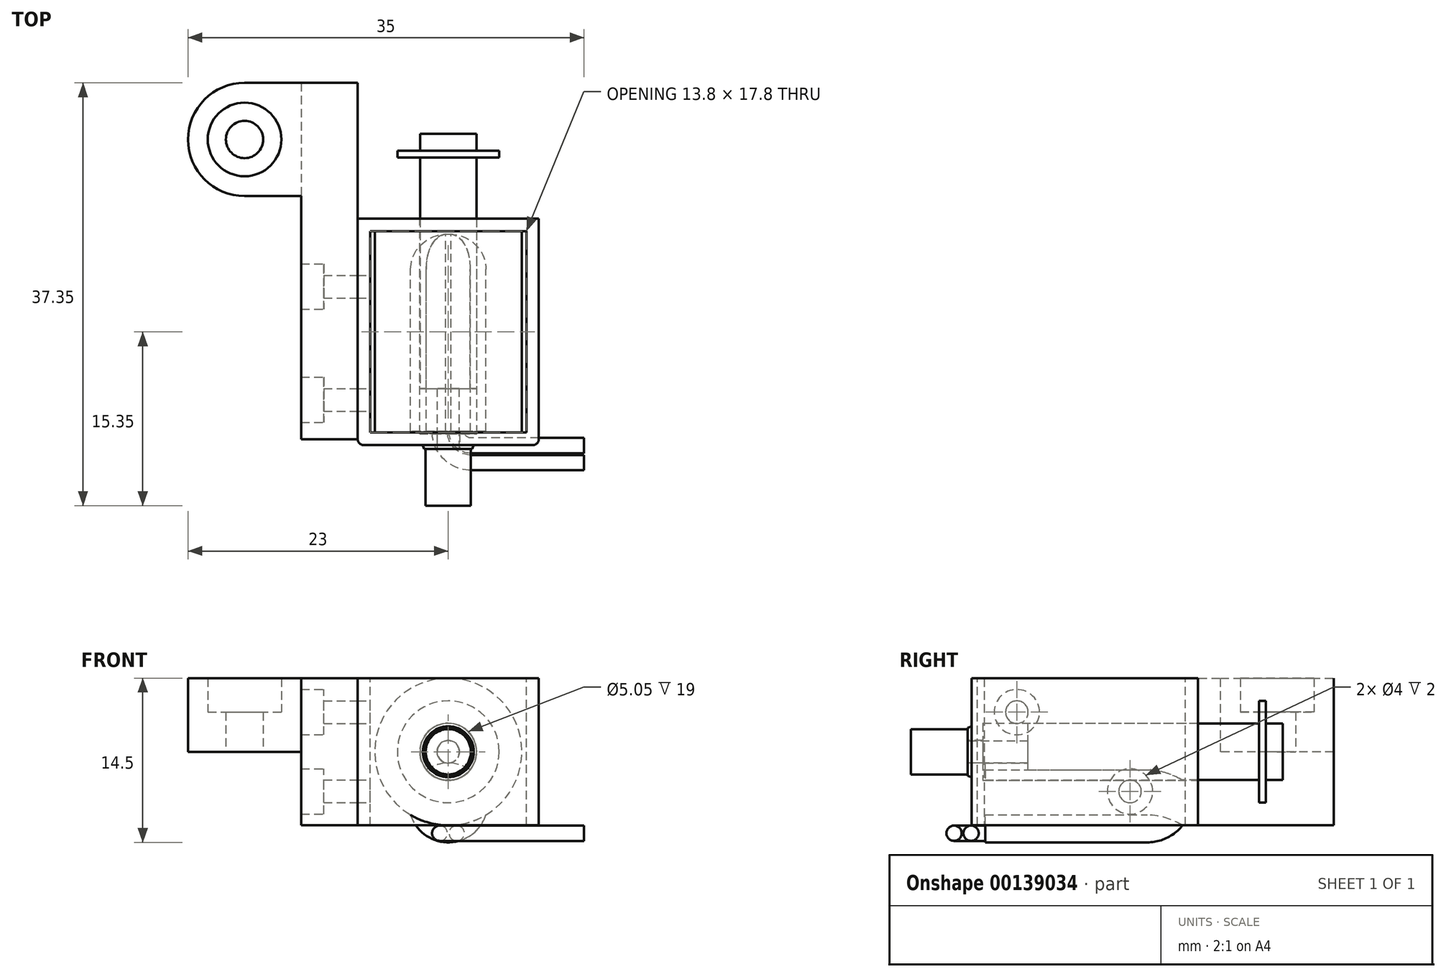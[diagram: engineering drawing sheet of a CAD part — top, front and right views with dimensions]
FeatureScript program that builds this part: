
annotation { "Feature Type Name" : "Feature", "Feature Type Description" : "" }
export const myFeature = defineFeature(function(context is Context, id is Id, definition is map)
    precondition{}
    {
        {
            var Q0;
            Q0=qCreatedBy(makeId("Front.planeOp"),FACE);
            var sketch = newSketch(context, id + "F0", { "sketchPlane" : qUnion([Q0])});
            skLineSegment(sketch, "E0.bottom", {"start": v(8, -6.5) * mm, "end": v(-8, -6.5) * mm});
            skLineSegment(sketch, "E0.top", {"start": v(8, 6.5) * mm, "end": v(-8, 6.5) * mm});
            skLineSegment(sketch, "E0.left", {"start": v(8, -6.5) * mm, "end": v(8, 6.5) * mm});
            skLineSegment(sketch, "E0.right", {"start": v(-8, -6.5) * mm, "end": v(-8, 6.5) * mm});
            skPoint(sketch, "E0.middle", {"position": v(0, 0) * mm});
            skSolve(sketch);
        }
        {
            var Q0;
            Q0 = qSketchRegion(id + "F0", true);
            extrude(context, id + "F1", {"entities" : qUnion([Q0]), "oppositeDirection" : true, "depth" : 20 * mm});
        }
        {
            var Q0;
            Q0=makeQuery(id+"F1.opExtrude","CAP_EDGE",EDGE,{"disambiguationData":[OSD([sQuery(id+"F0.wireOp",EDGE,"E0.right")])],"isStart":true});
            var Q1;
            Q1=makeQuery(id+"F1.opExtrude","CAP_EDGE",EDGE,{"disambiguationData":[OSD([sQuery(id+"F0.wireOp",EDGE,"E0.left")])],"isStart":true});
            fillet(context, id + "F2", {"entities" : qUnion([Q0, Q1]), "radius" : 0.5 * mm, "tangentPropagation" : true, "allowEdgeOverflow" : false});
        }
        {
            var Q0;
            Q0=makeQuery(id+"F1.opExtrude","SWEPT_FACE",FACE,{"disambiguationData":[OSD([sQuery(id+"F0.wireOp",EDGE,"E0.top")])]});
            var Q1;
            Q1=makeQuery(id+"F1.opExtrude","SWEPT_FACE",FACE,{"disambiguationData":[OSD([sQuery(id+"F0.wireOp",EDGE,"E0.bottom")])]});
            shell(context, id + "F3", {"entities" : qUnion([Q0, Q1]), "thickness" : 1.1 * mm});
        }
        {
            var Q0;
            {var subQ0=sQuery(id+"F0.wireOp",EDGE,"E0.right");var subQ1=sQuery(id+"F0.wireOp",EDGE,"E0.left");var subQ2=sQuery(id+"F0.wireOp",EDGE,"E0.top");var subQ3=sQuery(id+"F0.wireOp",EDGE,"E0.bottom");Q0=makeQuery(id+"F3.opShell","OFFSET_FACE",FACE,{"disambiguationData":[OSD([subQ3,subQ2,subQ1,subQ0]),TDD([makeQuery(id+"F1.opExtrude","CAP_FACE",FACE,{"disambiguationData":[OSD([subQ3,subQ2,subQ1,subQ0])],"isStart":true})])]});}
            var sketch = newSketch(context, id + "F4", { "sketchPlane" : qUnion([Q0])});
            skCircle(sketch, "E1", {"center": v(0, 0) * mm, "radius": 6.5 * mm});
            skSolve(sketch);
        }
        {
            var Q0;
            Q0 = qSketchRegion(id + "F4", true);
            extrude(context, id + "F5", {"entities" : qUnion([Q0]), "operationType" : NewBodyOperationType.ADD, "endBound" : BoundingType.UP_TO_NEXT, "depth" : 25 * mm});
        }
        {
            var Q0;
            Q0=makeQuery(id+"F1.opExtrude","CAP_FACE",FACE,{"disambiguationData":[OSD([sQuery(id+"F0.wireOp",EDGE,"E0.bottom"),sQuery(id+"F0.wireOp",EDGE,"E0.top"),sQuery(id+"F0.wireOp",EDGE,"E0.left"),sQuery(id+"F0.wireOp",EDGE,"E0.right")])],"isStart":true});
            var sketch = newSketch(context, id + "F6", { "sketchPlane" : qUnion([Q0])});
            skCircle(sketch, "E2", {"center": v(0, 0) * mm, "radius": 1 * mm});
            skSolve(sketch);
        }
        {
            var Q0;
            Q0=makeQuery(id+"F6.imprint","IMPRINT",FACE,{"disambiguationData":[TD([[makeQuery(id+"F6.imprint","IMPRINT",EDGE,{"derivedFrom":sQuery(id+"F6.wireOp",EDGE,"E2")}),-1.0]])]});
            var sketch = newSketch(context, id + "F7", { "sketchPlane" : qUnion([Q0])});
            skCircle(sketch, "E3", {"center": v(0, 0) * mm, "radius": 2.25 * mm});
            skSolve(sketch);
        }
        {
            var Q0;
            Q0 = qSketchRegion(id + "F7", true);
            extrude(context, id + "F8", {"entities" : qUnion([Q0]), "operationType" : NewBodyOperationType.ADD, "depth" : 0.35 * mm, "hasDraft" : true, "draftAngle" : 20 * degree, "draftPullDirection" : true});
        }
        {
            var Q0;
            Q0 = qSketchRegion(id + "F6", true);
            extrude(context, id + "F9", {"entities" : qUnion([Q0]), "operationType" : NewBodyOperationType.REMOVE, "endBound" : BoundingType.THROUGH_ALL, "oppositeDirection" : true, "depth" : 25 * mm, "hasSecondDirection" : true, "secondDirectionBound" : BoundingType.THROUGH_ALL, "secondDirectionOppositeDirection" : false, "secondDirectionDepth" : 25 * mm});
        }
        {
            var Q0;
            Q0=makeQuery(id+"F1.opExtrude","CAP_FACE",FACE,{"disambiguationData":[OSD([sQuery(id+"F0.wireOp",EDGE,"E0.bottom"),sQuery(id+"F0.wireOp",EDGE,"E0.top"),sQuery(id+"F0.wireOp",EDGE,"E0.left"),sQuery(id+"F0.wireOp",EDGE,"E0.right")])],"isStart":false});
            var sketch = newSketch(context, id + "F10", { "sketchPlane" : qUnion([Q0])});
            skCircle(sketch, "E4", {"center": v(0, 0) * mm, "radius": 2.52 * mm});
            skSolve(sketch);
        }
        {
            var Q0;
            Q0 = qSketchRegion(id + "F10", true);
            extrude(context, id + "F11", {"entities" : qUnion([Q0]), "operationType" : NewBodyOperationType.REMOVE, "oppositeDirection" : true, "depth" : 19 * mm});
        }
        {
            var Q0;
            Q0=makeQuery(id+"F1.opExtrude","CAP_FACE",FACE,{"disambiguationData":[OSD([sQuery(id+"F0.wireOp",EDGE,"E0.bottom"),sQuery(id+"F0.wireOp",EDGE,"E0.top"),sQuery(id+"F0.wireOp",EDGE,"E0.left"),sQuery(id+"F0.wireOp",EDGE,"E0.right")])],"isStart":false});
            var sketch = newSketch(context, id + "F12", { "sketchPlane" : qUnion([Q0])});
            skCircle(sketch, "E5", {"center": v(0, 0) * mm, "radius": 2.5 * mm});
            skSolve(sketch);
        }
        {
            var Q0;
            Q0 = qSketchRegion(id + "F12", true);
            extrude(context, id + "F13", {"entities" : qUnion([Q0]), "depth" : 7.5 * mm, "hasSecondDirection" : true, "secondDirectionOppositeDirection" : true, "secondDirectionDepth" : 15 * mm});
        }
        {
            var Q0;
            Q0=makeQuery(id+"F13.opExtrude","CAP_FACE",FACE,{"disambiguationData":[OSD([sQuery(id+"F12.wireOp",EDGE,"E5")])],"isStart":false});
            cPlane(context, id + "F14", {"entities" : qUnion([Q0]), "cplaneType" : CPlaneType.OFFSET, "offset" : 1.5 * mm, "oppositeDirection" : true, "width" : 150 * mm, "height" : 150 * mm});
        }
        {
            var Q0;
            Q0=qCreatedBy(id+"F14.planeOp",FACE);
            var sketch = newSketch(context, id + "F15", { "sketchPlane" : qUnion([Q0])});
            skCircle(sketch, "E6", {"center": v(0, 0) * mm, "radius": 4.5 * mm});
            skSolve(sketch);
        }
        {
            var Q0;
            Q0 = qSketchRegion(id + "F15", true);
            extrude(context, id + "F16", {"entities" : qUnion([Q0]), "operationType" : NewBodyOperationType.ADD, "oppositeDirection" : true, "depth" : 0.6 * mm});
        }
        {
            var Q0;
            Q0=makeQuery(id+"F13.opExtrude","CAP_FACE",FACE,{"disambiguationData":[OSD([sQuery(id+"F12.wireOp",EDGE,"E5")])],"isStart":true});
            var sketch = newSketch(context, id + "F17", { "sketchPlane" : qUnion([Q0])});
            skCircle(sketch, "E7", {"center": v(0, 0) * mm, "radius": 0.97 * mm});
            skSolve(sketch);
        }
        {
            var Q0;
            Q0 = qSketchRegion(id + "F17", true);
            extrude(context, id + "F18", {"entities" : qUnion([Q0]), "operationType" : NewBodyOperationType.ADD, "depth" : 10.35 * mm});
        }
        {
            var Q0;
            Q0=makeQuery(id+"F18.opExtrude","CAP_FACE",FACE,{"disambiguationData":[OSD([sQuery(id+"F17.wireOp",EDGE,"E7")])],"isStart":false});
            var sketch = newSketch(context, id + "F19", { "sketchPlane" : qUnion([Q0])});
            skCircle(sketch, "E8", {"center": v(0, 0) * mm, "radius": 2 * mm});
            skSolve(sketch);
        }
        {
            var Q0;
            Q0=makeQuery(id+"F19.imprint","IMPRINT",FACE,{"disambiguationData":[TD([[makeQuery(id+"F19.imprint","IMPRINT",EDGE,{"derivedFrom":sQuery(id+"F19.wireOp",EDGE,"E8")}),1.0]])]});
            extrude(context, id + "F20", {"entities" : qUnion([Q0]), "operationType" : NewBodyOperationType.ADD, "oppositeDirection" : true, "depth" : 5 * mm});
        }
        {
            var Q0;
            Q0=makeQuery(id+"F1.opExtrude","SWEPT_FACE",FACE,{"disambiguationData":[OSD([sQuery(id+"F0.wireOp",EDGE,"E0.right")])]});
            var sketch = newSketch(context, id + "F21", { "sketchPlane" : qUnion([Q0])});
            skPoint(sketch, "E9", {"position": v(-14, -3.5) * mm});
            skPoint(sketch, "E10", {"position": v(-4, 3.5) * mm});
            skLineSegment(sketch, "E11", {"start": v(-20, 0) * mm, "end": v(-0.5, 0) * mm, "construction": true});
            skSolve(sketch);
        }
        {
            var Q0;
            Q0=sQuery(id+"F21.wireOp",VERTEX,"E10");
            var Q1;
            Q1=sQuery(id+"F21.wireOp",VERTEX,"E9");
            var Q2;
            Q2=makeQuery(id+"F1.opExtrude","SWEPT_BODY",BODY,{"disambiguationData":[OSD([sQuery(id+"F0.wireOp",EDGE,"E0.bottom"),sQuery(id+"F0.wireOp",EDGE,"E0.top"),sQuery(id+"F0.wireOp",EDGE,"E0.left"),sQuery(id+"F0.wireOp",EDGE,"E0.right")])]});
            hole(context, id + "F22", {"style" : HoleStyle.SIMPLE, "endStyle" : HoleEndStyle.BLIND, "holeDiameter" : 2 * mm, "holeDepth" : 1.5 * mm, "locations" : qUnion([Q0, Q1]), "scope" : qUnion([Q2]), "startStyle" : HoleStartStyle.SKETCH});
        }
        {
            var Q0;
            Q0=qCreatedBy(makeId("Right.planeOp"),FACE);
            var sketch = newSketch(context, id + "F23", { "sketchPlane" : qUnion([Q0])});
            skLineSegment(sketch, "E12", {"start": v(18.65, -6.5) * mm, "end": v(1.2, -6.5) * mm});
            skLineSegment(sketch, "E13", {"start": v(15.53, -8) * mm, "end": v(1.2, -8) * mm});
            skLineSegment(sketch, "E14", {"start": v(1.2, -8) * mm, "end": v(1.2, -6.5) * mm});
            skArc(sketch, "E15", {"start": v(15.53, -8) * mm, "mid": v(17.26, -7.6) * mm, "end": v(18.65, -6.5) * mm});
            skLineSegment(sketch, "E16.0", {"start": v(18.65, -4.5) * mm, "end": v(1.2, -4.5) * mm, "construction": true});
            skLineSegment(sketch, "E17.0", {"start": v(18.65, 0.5) * mm, "end": v(1.2, 0.5) * mm, "construction": true});
            skSolve(sketch);
        }
        {
            var Q0;
            Q0 = qSketchRegion(id + "F23", true);
            var Q1;
            Q1=sQuery(id+"F23.wireOp",EDGE,"E16.0");
            revolve(context, id + "F24", {"operationType" : NewBodyOperationType.ADD, "entities" : qUnion([Q0]), "axis" : qUnion([Q1]), "revolveType" : RevolveType.FULL});
        }
        {
            var Q0;
            Q0=makeQuery(id+"F1.opExtrude","SWEPT_FACE",FACE,{"disambiguationData":[OSD([sQuery(id+"F0.wireOp",EDGE,"E0.right")])]});
            var sketch = newSketch(context, id + "F25", { "sketchPlane" : qUnion([Q0])});
            skLineSegment(sketch, "E18.bottom", {"start": v(-0.5, -6.5) * mm, "end": v(-32, -6.5) * mm});
            skLineSegment(sketch, "E18.top", {"start": v(-0.5, 6.5) * mm, "end": v(-32, 6.5) * mm});
            skLineSegment(sketch, "E18.left", {"start": v(-0.5, -6.5) * mm, "end": v(-0.5, 6.5) * mm});
            skLineSegment(sketch, "E18.right", {"start": v(-32, -6.5) * mm, "end": v(-32, 6.5) * mm});
            skSolve(sketch);
        }
        {
            var Q0;
            Q0 = qSketchRegion(id + "F25", true);
            extrude(context, id + "F26", {"entities" : qUnion([Q0]), "depth" : 5 * mm});
        }
        {
            var Q0;
            Q0=makeQuery(id+"F26.opExtrude","CAP_FACE",FACE,{"disambiguationData":[OSD([sQuery(id+"F25.wireOp",EDGE,"E18.bottom"),sQuery(id+"F25.wireOp",EDGE,"E18.top"),sQuery(id+"F25.wireOp",EDGE,"E18.left"),sQuery(id+"F25.wireOp",EDGE,"E18.right")])],"isStart":false});
            var sketch = newSketch(context, id + "F27", { "sketchPlane" : qUnion([Q0])});
            skPoint(sketch, "E19.0", {"position": v(-4, 3.5) * mm});
            skPoint(sketch, "E20.0", {"position": v(-14, -3.5) * mm});
            skSolve(sketch);
        }
        {
            var Q0;
            Q0=sQuery(id+"F27.wireOp",VERTEX,"E19.0");
            var Q1;
            Q1=sQuery(id+"F27.wireOp",VERTEX,"E20.0");
            var Q2;
            Q2=makeQuery(id+"F26.opExtrude","SWEPT_BODY",BODY,{"disambiguationData":[OSD([sQuery(id+"F25.wireOp",EDGE,"E18.bottom"),sQuery(id+"F25.wireOp",EDGE,"E18.top"),sQuery(id+"F25.wireOp",EDGE,"E18.left"),sQuery(id+"F25.wireOp",EDGE,"E18.right")])]});
            hole(context, id + "F28", {"style" : HoleStyle.C_BORE, "endStyle" : HoleEndStyle.BLIND, "holeDiameter" : 2 * mm, "cBoreDiameter" : 4 * mm, "cBoreDepth" : 2 * mm, "holeDepth" : 10 * mm, "locations" : qUnion([Q0, Q1]), "scope" : qUnion([Q2]), "startStyle" : HoleStartStyle.SKETCH});
        }
        {
            var Q0;
            Q0=makeQuery(id+"F26.opExtrude","CAP_FACE",FACE,{"disambiguationData":[OSD([sQuery(id+"F25.wireOp",EDGE,"E18.bottom"),sQuery(id+"F25.wireOp",EDGE,"E18.top"),sQuery(id+"F25.wireOp",EDGE,"E18.left"),sQuery(id+"F25.wireOp",EDGE,"E18.right")])],"isStart":false});
            var sketch = newSketch(context, id + "F29", { "sketchPlane" : qUnion([Q0])});
            skLineSegment(sketch, "E21.bottom", {"start": v(-32, 6.5) * mm, "end": v(-22, 6.5) * mm});
            skLineSegment(sketch, "E21.top", {"start": v(-32, 0) * mm, "end": v(-22, 0) * mm});
            skLineSegment(sketch, "E21.left", {"start": v(-32, 0) * mm, "end": v(-32, 6.5) * mm});
            skLineSegment(sketch, "E21.right", {"start": v(-22, 0) * mm, "end": v(-22, 6.5) * mm});
            skSolve(sketch);
        }
        {
            var Q0;
            Q0 = qSketchRegion(id + "F29", true);
            extrude(context, id + "F30", {"entities" : qUnion([Q0]), "operationType" : NewBodyOperationType.ADD, "depth" : 10 * mm});
        }
        {
            var Q0;
            Q0=makeQuery(id+"F30.opExtrude","CAP_EDGE",EDGE,{"disambiguationData":[OSD([sQuery(id+"F29.wireOp",EDGE,"E21.right")])],"isStart":false});
            var Q1;
            Q1=makeQuery(id+"F30.opExtrude","CAP_EDGE",EDGE,{"disambiguationData":[OSD([sQuery(id+"F29.wireOp",EDGE,"E21.left")])],"isStart":false});
            fillet(context, id + "F31", {"entities" : qUnion([Q0, Q1]), "radius" : 5 * mm, "tangentPropagation" : true, "allowEdgeOverflow" : false});
        }
        {
            var Q0;
            Q0=makeQuery(id+"F30.boolean.opBoolean","MERGE",FACE,{"derivedFrom":[makeQuery(id+"F26.opExtrude","SWEPT_FACE",FACE,{"disambiguationData":[OSD([sQuery(id+"F25.wireOp",EDGE,"E18.top")])]}),makeQuery(id+"F30.opExtrude","SWEPT_FACE",FACE,{"disambiguationData":[OSD([sQuery(id+"F29.wireOp",EDGE,"E21.bottom")])]})]});
            var sketch = newSketch(context, id + "F32", { "sketchPlane" : qUnion([Q0])});
            skPoint(sketch, "E22", {"position": v(-18, 27) * mm});
            skSolve(sketch);
        }
        {
            var Q0;
            Q0=sQuery(id+"F32.wireOp",VERTEX,"E22");
            var Q1;
            Q1=makeQuery(id+"F26.opExtrude","SWEPT_BODY",BODY,{"disambiguationData":[OSD([sQuery(id+"F25.wireOp",EDGE,"E18.bottom"),sQuery(id+"F25.wireOp",EDGE,"E18.top"),sQuery(id+"F25.wireOp",EDGE,"E18.left"),sQuery(id+"F25.wireOp",EDGE,"E18.right")])]});
            hole(context, id + "F33", {"style" : HoleStyle.C_BORE, "endStyle" : HoleEndStyle.BLIND, "standardTappedOrClearance" : lookupTablePath({ "standard" : "ISO", "fit" : "Normal", "size" : "M3", "type" : "Clearance" }), "standardBlindInLast" : lookupTablePath({ "fit" : "Standard", "standard" : "ISO", "size" : "M3", "type" : "Clearance" }), "holeDiameter" : 3.3 * mm, "cBoreDiameter" : 6.5 * mm, "cBoreDepth" : 3 * mm, "holeDepth" : 10 * mm, "locations" : qUnion([Q0]), "scope" : qUnion([Q1]), "startStyle" : HoleStartStyle.SKETCH});
        }
        {
            var Q0;
            Q0=makeQuery(id+"F24.boolean.opBoolean","SPLIT",FACE,{"disambiguationData":[TD([makeQuery(id+"F5.opExtrude","SWEPT_FACE",FACE,{"disambiguationData":[OSD([sQuery(id+"F4.wireOp",EDGE,"E1")])]})])],"derivedFrom":makeQuery(id+"F24.opRevolve","SWEPT_FACE",FACE,{"disambiguationData":[OSD([sQuery(id+"F23.wireOp",EDGE,"E14")])]})});
            var sketch = newSketch(context, id + "F34", { "sketchPlane" : qUnion([Q0])});
            skLineSegment(sketch, "E23", {"start": v(0, 0) * mm, "end": v(0, -7.2) * mm, "construction": true});
            skPoint(sketch, "E23.endSnap0", {"position": v(0, -6.5) * mm});
            skLineSegment(sketch, "E24", {"start": v(-0.75, -7.2) * mm, "end": v(0.75, -7.2) * mm, "construction": true});
            skCircle(sketch, "E25", {"center": v(-0.75, -7.2) * mm, "radius": 0.68 * mm});
            skCircle(sketch, "E26", {"center": v(0.75, -7.2) * mm, "radius": 0.68 * mm});
            skLineSegment(sketch, "E27.0", {"start": v(2, 0) * mm, "end": v(2, -7.08) * mm, "construction": true});
            skSolve(sketch);
        }
        {
            var Q0;
            {var subQ0=sQuery(id+"F34.wireOp",EDGE,"E25");var subQ1=sQuery(id+"F23.wireOp",EDGE,"E13");var subQ2=sQuery(id+"F23.wireOp",EDGE,"E14");var subQ3=makeQuery(id+"F24.boolean.opBoolean","SPLIT",EDGE,{"disambiguationData":[TD([makeQuery(id+"F5.opExtrude","SWEPT_FACE",FACE,{"disambiguationData":[OSD([sQuery(id+"F4.wireOp",EDGE,"E1")])]})])],"derivedFrom":makeQuery(id+"F24.opRevolve","SWEPT_EDGE",EDGE,{"disambiguationData":[OSD([subQ1,subQ2])]})});var subQ4=makeQuery(id+"F34.imprint","INTERSECT",VERTEX,{"disambiguationData":[OD(0.0)],"derivedFrom":[subQ3,subQ0]});Q0=makeQuery(id+"F34.imprint","IMPRINT",FACE,{"disambiguationData":[TD([[makeQuery(id+"F34.imprint","IMPRINT",EDGE,{"disambiguationData":[TD([[subQ4,1.0]])],"derivedFrom":subQ0}),1.0]])]});}
            var Q1;
            {var subQ0=sQuery(id+"F34.wireOp",EDGE,"E26");var subQ1=sQuery(id+"F23.wireOp",EDGE,"E13");var subQ2=sQuery(id+"F23.wireOp",EDGE,"E14");var subQ3=makeQuery(id+"F24.boolean.opBoolean","SPLIT",EDGE,{"disambiguationData":[TD([makeQuery(id+"F5.opExtrude","SWEPT_FACE",FACE,{"disambiguationData":[OSD([sQuery(id+"F4.wireOp",EDGE,"E1")])]})])],"derivedFrom":makeQuery(id+"F24.opRevolve","SWEPT_EDGE",EDGE,{"disambiguationData":[OSD([subQ1,subQ2])]})});var subQ4=makeQuery(id+"F34.imprint","INTERSECT",VERTEX,{"disambiguationData":[OD(0.0)],"derivedFrom":[subQ3,subQ0]});Q1=makeQuery(id+"F34.imprint","IMPRINT",FACE,{"disambiguationData":[TD([[makeQuery(id+"F34.imprint","IMPRINT",EDGE,{"disambiguationData":[TD([[subQ4,-1.0]])],"derivedFrom":subQ0}),1.0]])]});}
            var Q2;
            Q2=sQuery(id+"F34.wireOp",EDGE,"E27.0");
            revolve(context, id + "F35", {"operationType" : NewBodyOperationType.ADD, "entities" : qUnion([Q0, Q1]), "axis" : qUnion([Q2]), "revolveType" : RevolveType.ONE_DIRECTION, "oppositeDirection" : true, "angle" : 90 * degree});
        }
        {
            var Q0;
            Q0=makeQuery(id+"F35.opRevolve","CAP_FACE",FACE,{"disambiguationData":[OSD([sQuery(id+"F23.wireOp",EDGE,"E13"),sQuery(id+"F23.wireOp",EDGE,"E14"),sQuery(id+"F34.wireOp",EDGE,"E25")])],"isStart":false});
            extrude(context, id + "F36", {"entities" : qUnion([Q0]), "operationType" : NewBodyOperationType.ADD, "depth" : 10 * mm});
        }
        {
            var Q0;
            Q0=makeQuery(id+"F35.opRevolve","CAP_FACE",FACE,{"disambiguationData":[OSD([sQuery(id+"F23.wireOp",EDGE,"E13"),sQuery(id+"F23.wireOp",EDGE,"E14"),sQuery(id+"F34.wireOp",EDGE,"E26")])],"isStart":false});
            extrude(context, id + "F37", {"entities" : qUnion([Q0]), "operationType" : NewBodyOperationType.ADD, "depth" : 10 * mm});
        }
    });
